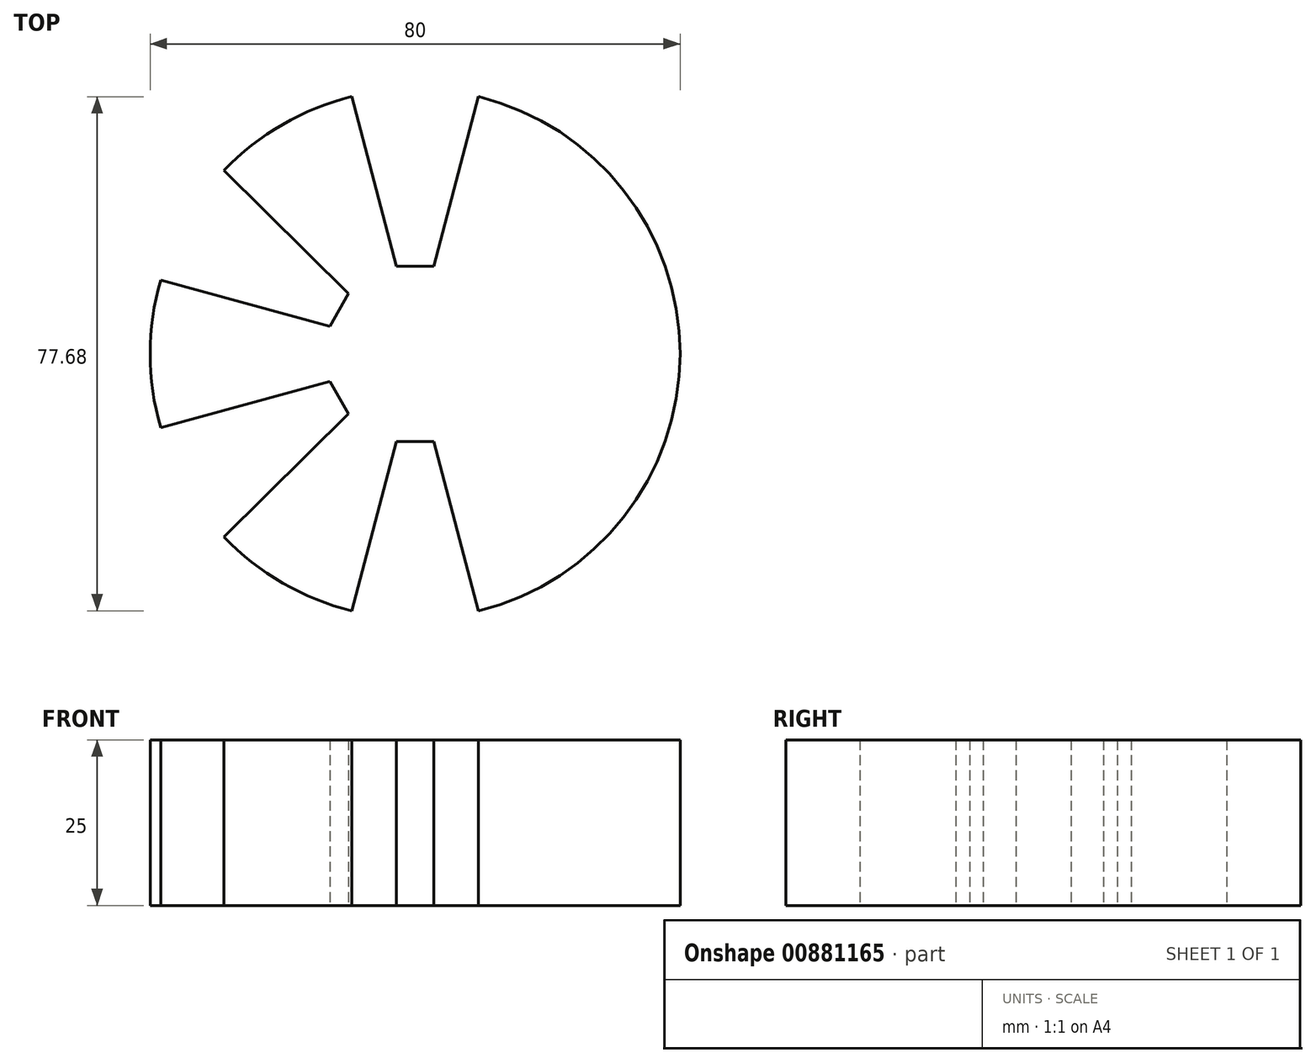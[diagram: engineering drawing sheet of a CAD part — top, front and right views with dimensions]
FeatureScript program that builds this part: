
annotation { "Feature Type Name" : "Feature", "Feature Type Description" : "" }
export const myFeature = defineFeature(function(context is Context, id is Id, definition is map)
    precondition{}
    {
        {
            var Q0;
            Q0=qCreatedBy(makeId("Top.planeOp"),FACE);
            var sketch = newSketch(context, id + "F0", { "sketchPlane" : qUnion([Q0])});
            skCircle(sketch, "E0", {"center": v(0, 0) * mm, "radius": 40 * mm});
            skLineSegment(sketch, "E1", {"start": v(-9.55, 38.84) * mm, "end": v(-2.83, 13.24) * mm});
            skLineSegment(sketch, "E2", {"start": v(-2.83, 13.24) * mm, "end": v(0, 13.24) * mm});
            skLineSegment(sketch, "E3.MirrorCS", {"start": v(9.55, 38.84) * mm, "end": v(2.83, 13.24) * mm});
            skLineSegment(sketch, "E4.MirrorCS", {"start": v(2.83, 13.24) * mm, "end": v(0, 13.24) * mm});
            skLineSegment(sketch, "E5.MirrorCS", {"start": v(-9.55, -38.84) * mm, "end": v(-2.83, -13.24) * mm});
            skLineSegment(sketch, "E6.MirrorCS", {"start": v(-2.83, -13.24) * mm, "end": v(0, -13.24) * mm});
            skLineSegment(sketch, "E7.MirrorCS", {"start": v(2.83, -13.24) * mm, "end": v(0, -13.24) * mm});
            skLineSegment(sketch, "E8.MirrorCS", {"start": v(9.55, -38.84) * mm, "end": v(2.83, -13.24) * mm});
            skLineSegment(sketch, "E9.MirrorCS", {"start": v(-28.86, 27.7) * mm, "end": v(-10.05, 9.07) * mm});
            skLineSegment(sketch, "E10.MirrorCS", {"start": v(-10.05, 9.07) * mm, "end": v(-11.46, 6.62) * mm});
            skLineSegment(sketch, "E11.MirrorCS", {"start": v(-12.88, 4.17) * mm, "end": v(-11.46, 6.62) * mm});
            skLineSegment(sketch, "E12.MirrorCS", {"start": v(-38.41, 11.15) * mm, "end": v(-12.88, 4.17) * mm});
            skLineSegment(sketch, "E13", {"start": v(0, 0) * mm, "end": v(-20, -34.64) * mm});
            skLineSegment(sketch, "E14.MirrorCS", {"start": v(-28.86, -27.7) * mm, "end": v(-10.05, -9.07) * mm});
            skLineSegment(sketch, "E15.MirrorCS", {"start": v(-10.05, -9.07) * mm, "end": v(-11.46, -6.62) * mm});
            skLineSegment(sketch, "E16.MirrorCS", {"start": v(-12.88, -4.17) * mm, "end": v(-11.46, -6.62) * mm});
            skLineSegment(sketch, "E17.MirrorCS", {"start": v(-38.41, -11.15) * mm, "end": v(-12.88, -4.17) * mm});
            skSolve(sketch);
        }
        {
            var Q0;
            {var subQ1=sQuery(id+"F0.wireOp",EDGE,"E1");Q0=makeQuery(id+"F0.imprint","IMPRINT",FACE,{"disambiguationData":[TD([[makeQuery(id+"F0.imprint","IMPRINT",EDGE,{"derivedFrom":subQ1}),-1.0]])]});}
            extrude(context, id + "F1", {"entities" : qUnion([Q0]), "depth" : 25 * mm, "offsetDistance" : 25 * mm});
        }
    });
